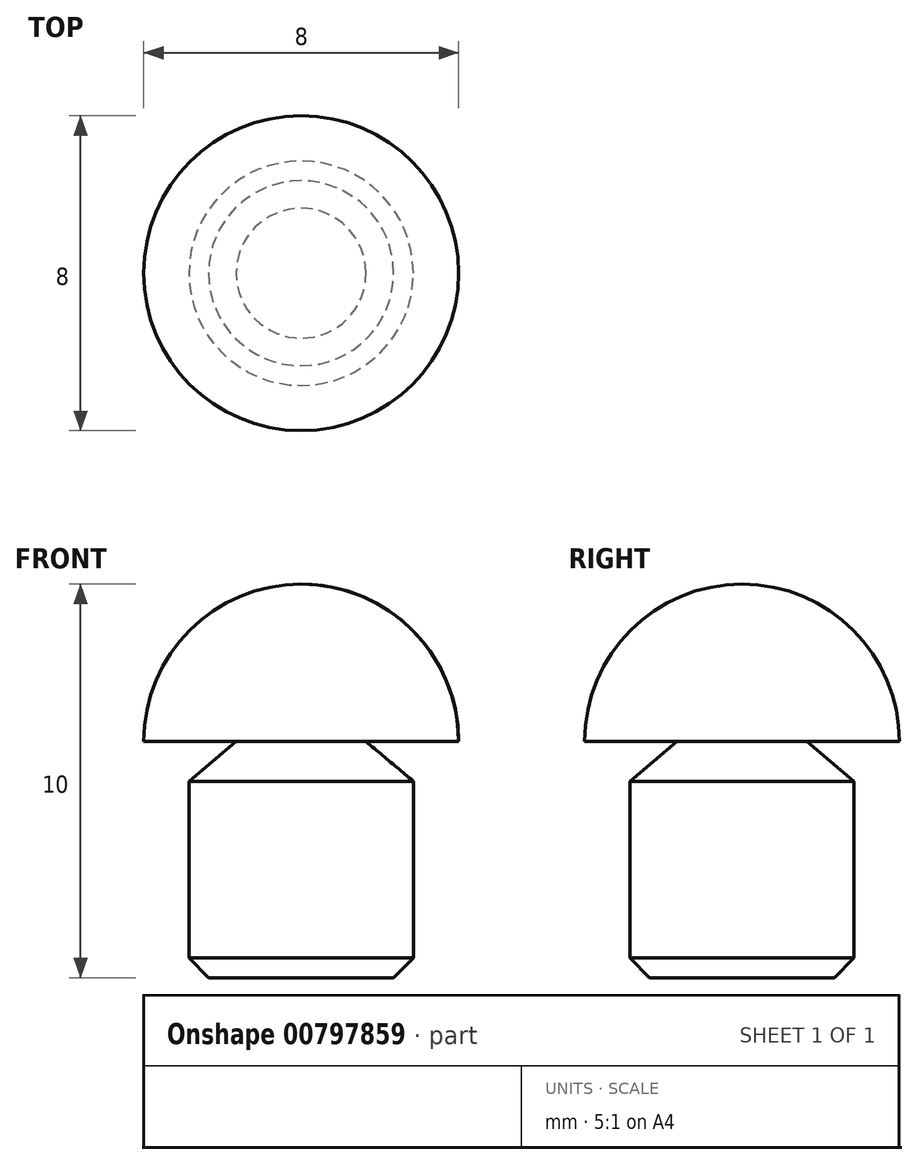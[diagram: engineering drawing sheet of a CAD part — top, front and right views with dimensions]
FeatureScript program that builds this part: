
annotation { "Feature Type Name" : "Feature", "Feature Type Description" : "" }
export const myFeature = defineFeature(function(context is Context, id is Id, definition is map)
    precondition{}
    {
        {
            var Q0;
            Q0=qCreatedBy(makeId("Top.planeOp"),FACE);
            var sketch = newSketch(context, id + "F0", { "sketchPlane" : qUnion([Q0])});
            skCircle(sketch, "E0", {"center": v(0, 0) * mm, "radius": 4 * mm});
            skCircle(sketch, "E1", {"center": v(0, 0) * mm, "radius": 2.85 * mm});
            skSolve(sketch);
        }
        {
            var Q0;
            Q0=makeQuery(id+"F0.imprint","IMPRINT",FACE,{"disambiguationData":[TD([[makeQuery(id+"F0.imprint","IMPRINT",EDGE,{"derivedFrom":sQuery(id+"F0.wireOp",EDGE,"E0")}),1.0]])]});
            var Q1;
            Q1=makeQuery(id+"F0.imprint","IMPRINT",FACE,{"disambiguationData":[TD([[makeQuery(id+"F0.imprint","IMPRINT",EDGE,{"derivedFrom":sQuery(id+"F0.wireOp",EDGE,"E1")}),1.0]])]});
            extrude(context, id + "F1", {"entities" : qUnion([Q0, Q1]), "depth" : 4 * mm, "offsetDistance" : 25 * mm});
        }
        {
            var Q0;
            Q0=makeQuery(id+"F0.imprint","IMPRINT",FACE,{"disambiguationData":[TD([[makeQuery(id+"F0.imprint","IMPRINT",EDGE,{"derivedFrom":sQuery(id+"F0.wireOp",EDGE,"E1")}),1.0]])]});
            var Q1;
            Q1=sQuery(id+"F0.wireOp",EDGE,"E1");
            extrude(context, id + "F2", {"entities" : qUnion([Q0]), "surfaceEntities" : qUnion([Q1]), "oppositeDirection" : true, "depth" : 6 * mm, "offsetDistance" : 25 * mm});
        }
        {
            var Q0;
            Q0=makeQuery(id+"F1.opExtrude","CAP_EDGE",EDGE,{"disambiguationData":[OSD([sQuery(id+"F0.wireOp",EDGE,"E0")])],"isStart":false});
            fillet(context, id + "F3", {"entities" : qUnion([Q0]), "radius" : 4 * mm, "tangentPropagation" : true, "allowEdgeOverflow" : false});
        }
        {
            var Q0;
            Q0=makeQuery(id+"F2.opExtrude","CAP_EDGE",EDGE,{"disambiguationData":[OSD([sQuery(id+"F0.wireOp",EDGE,"E1")])],"isStart":false});
            chamfer(context, id + "F4", {"entities" : qUnion([Q0]), "width" : 0.5 * mm, "tangentPropagation" : true});
        }
        {
            var Q0;
            Q0=makeQuery(id+"F2.opExtrude","CAP_EDGE",EDGE,{"disambiguationData":[OSD([sQuery(id+"F0.wireOp",EDGE,"E1")])],"isStart":true});
            chamfer(context, id + "F5", {"entities" : qUnion([Q0]), "chamferType" : ChamferType.OFFSET_ANGLE, "width" : 1.2 * mm, "oppositeDirection" : false, "angle" : 40 * degree, "tangentPropagation" : true});
        }
    });
